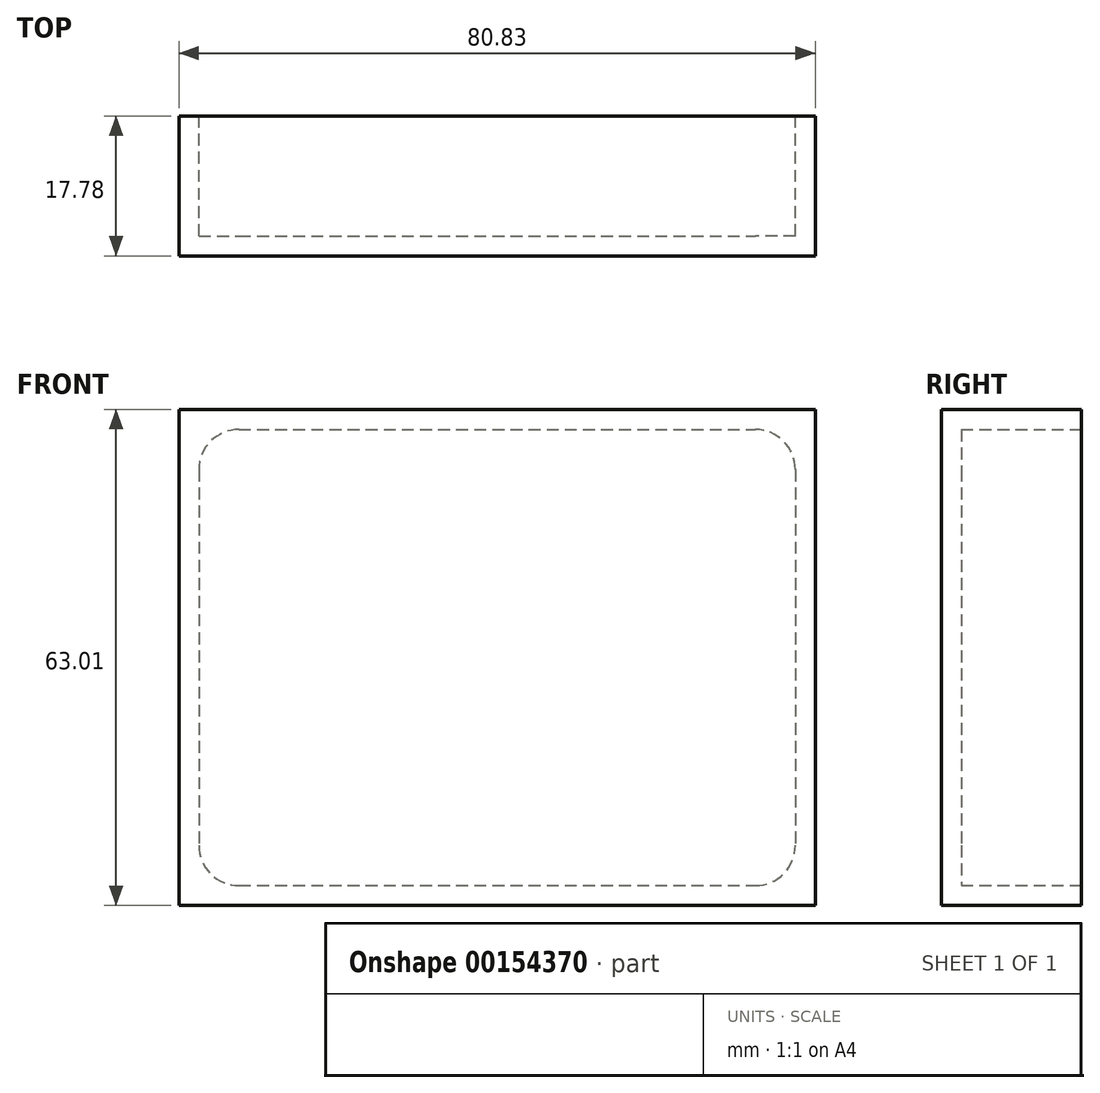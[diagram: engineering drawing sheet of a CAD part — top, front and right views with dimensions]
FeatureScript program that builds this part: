
annotation { "Feature Type Name" : "Feature", "Feature Type Description" : "" }
export const myFeature = defineFeature(function(context is Context, id is Id, definition is map)
    precondition{}
    {
        {
            var Q0;
            Q0=qCreatedBy(makeId("Front.planeOp"),FACE);
            var sketch = newSketch(context, id + "F0", { "sketchPlane" : qUnion([Q0])});
            skLineSegment(sketch, "E0.bottom", {"start": v(-35.11, 24.18) * mm, "end": v(45.72, 24.18) * mm});
            skLineSegment(sketch, "E0.top", {"start": v(-35.11, -38.83) * mm, "end": v(45.72, -38.83) * mm});
            skLineSegment(sketch, "E0.left", {"start": v(-35.11, 24.18) * mm, "end": v(-35.11, -38.83) * mm});
            skLineSegment(sketch, "E0.right", {"start": v(45.72, 24.18) * mm, "end": v(45.72, -38.83) * mm});
            skSolve(sketch);
        }
        {
            var Q0;
            Q0 = qSketchRegion(id + "F0", true);
            extrude(context, id + "F1", {"entities" : qUnion([Q0]), "depth" : 17.78 * mm});
        }
        {
            var Q0;
            Q0=makeQuery(id+"F1.opExtrude","CAP_FACE",FACE,{"disambiguationData":[OSD([sQuery(id+"F0.wireOp",EDGE,"E0.bottom"),sQuery(id+"F0.wireOp",EDGE,"E0.top"),sQuery(id+"F0.wireOp",EDGE,"E0.left"),sQuery(id+"F0.wireOp",EDGE,"E0.right")])],"isStart":true});
            shell(context, id + "F2", {"entities" : qUnion([Q0]), "thickness" : 2.54 * mm});
        }
        {
            var Q0;
            Q0=makeQuery(id+"F2.opShell","OFFSET_EDGE",EDGE,{"disambiguationData":[OSD([sQuery(id+"F0.wireOp",EDGE,"E0.bottom"),sQuery(id+"F0.wireOp",EDGE,"E0.left")])]});
            var Q1;
            Q1=makeQuery(id+"F2.opShell","OFFSET_EDGE",EDGE,{"disambiguationData":[OSD([sQuery(id+"F0.wireOp",EDGE,"E0.bottom"),sQuery(id+"F0.wireOp",EDGE,"E0.right")])]});
            var Q2;
            Q2=makeQuery(id+"F2.opShell","OFFSET_EDGE",EDGE,{"disambiguationData":[OSD([sQuery(id+"F0.wireOp",EDGE,"E0.top"),sQuery(id+"F0.wireOp",EDGE,"E0.right")])]});
            var Q3;
            Q3=makeQuery(id+"F2.opShell","OFFSET_EDGE",EDGE,{"disambiguationData":[OSD([sQuery(id+"F0.wireOp",EDGE,"E0.top"),sQuery(id+"F0.wireOp",EDGE,"E0.left")])]});
            fillet(context, id + "F3", {"entities" : qUnion([Q0, Q1, Q2, Q3]), "radius" : 5.08 * mm, "tangentPropagation" : true, "allowEdgeOverflow" : false});
        }
    });
